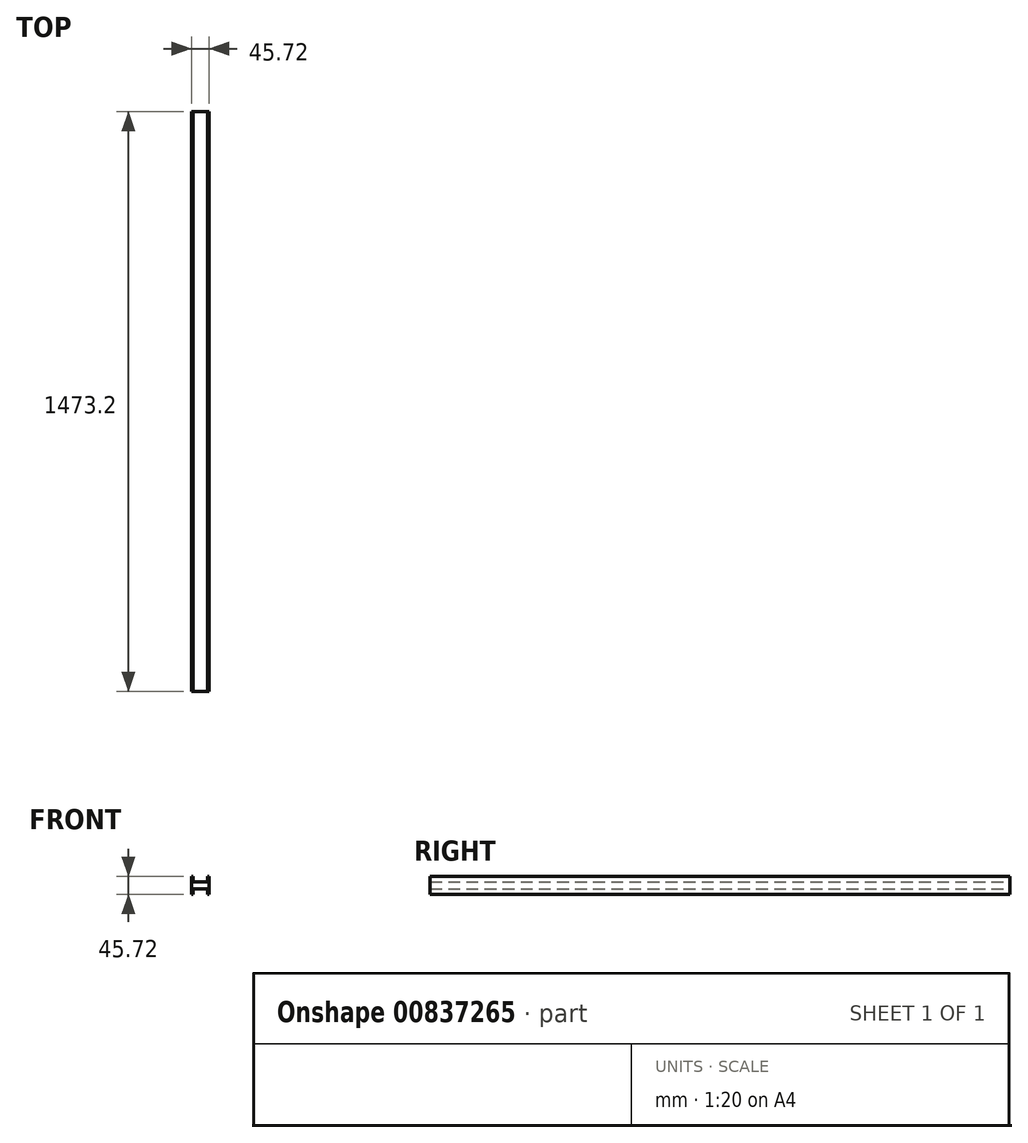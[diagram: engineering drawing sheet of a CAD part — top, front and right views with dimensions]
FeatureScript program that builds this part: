
annotation { "Feature Type Name" : "Feature", "Feature Type Description" : "" }
export const myFeature = defineFeature(function(context is Context, id is Id, definition is map)
    precondition{}
    {
        {
            var Q0;
            Q0=qCreatedBy(makeId("Front.planeOp"),FACE);
            var sketch = newSketch(context, id + "F0", { "sketchPlane" : qUnion([Q0])});
            skLineSegment(sketch, "E0.bottom", {"start": v(22.86, 22.86) * mm, "end": v(17.8, 22.86) * mm});
            skLineSegment(sketch, "E0.top", {"start": v(22.86, -22.86) * mm, "end": v(17.8, -22.86) * mm});
            skLineSegment(sketch, "E0.left", {"start": v(22.86, 22.86) * mm, "end": v(22.86, -22.86) * mm});
            skLineSegment(sketch, "E0.right", {"start": v(-22.86, 22.86) * mm, "end": v(-22.86, -22.86) * mm});
            skPoint(sketch, "E0.middle", {"position": v(0, 0) * mm});
            skLineSegment(sketch, "E1.top", {"start": v(-18.22, 8.64) * mm, "end": v(17.8, 8.64) * mm});
            skLineSegment(sketch, "E1.left", {"start": v(-18.22, 22.86) * mm, "end": v(-18.22, 8.64) * mm});
            skLineSegment(sketch, "E1.right", {"start": v(17.8, 22.86) * mm, "end": v(17.8, 8.64) * mm});
            skLineSegment(sketch, "E2", {"start": v(-65.42, 0) * mm, "end": v(65.2, 0) * mm, "construction": true});
            skLineSegment(sketch, "E3.MirrorCS", {"start": v(-18.22, -22.86) * mm, "end": v(-18.22, -8.64) * mm});
            skLineSegment(sketch, "E4.MirrorCS", {"start": v(-18.22, -8.64) * mm, "end": v(17.8, -8.64) * mm});
            skLineSegment(sketch, "E5.MirrorCS", {"start": v(17.8, -22.86) * mm, "end": v(17.8, -8.64) * mm});
            skLineSegment(sketch, "E6.trimOffspring", {"start": v(-18.22, 22.86) * mm, "end": v(-22.86, 22.86) * mm});
            skPoint(sketch, "E7.orphan", {"position": v(17.8, -31.29) * mm});
            skLineSegment(sketch, "E8.trimOffspring", {"start": v(-18.22, -22.86) * mm, "end": v(-22.86, -22.86) * mm});
            skPoint(sketch, "E9.orphan", {"position": v(-18.22, -31.29) * mm});
            skSolve(sketch);
        }
        {
            var Q0;
            Q0=qSketchRegion(id+"F0",true);
            extrude(context, id + "F1", {"entities" : qUnion([Q0]), "endBound" : BoundingType.SYMMETRIC, "depth" : 1473.2 * mm, "offsetDistance" : 25.4 * mm});
        }
    });
